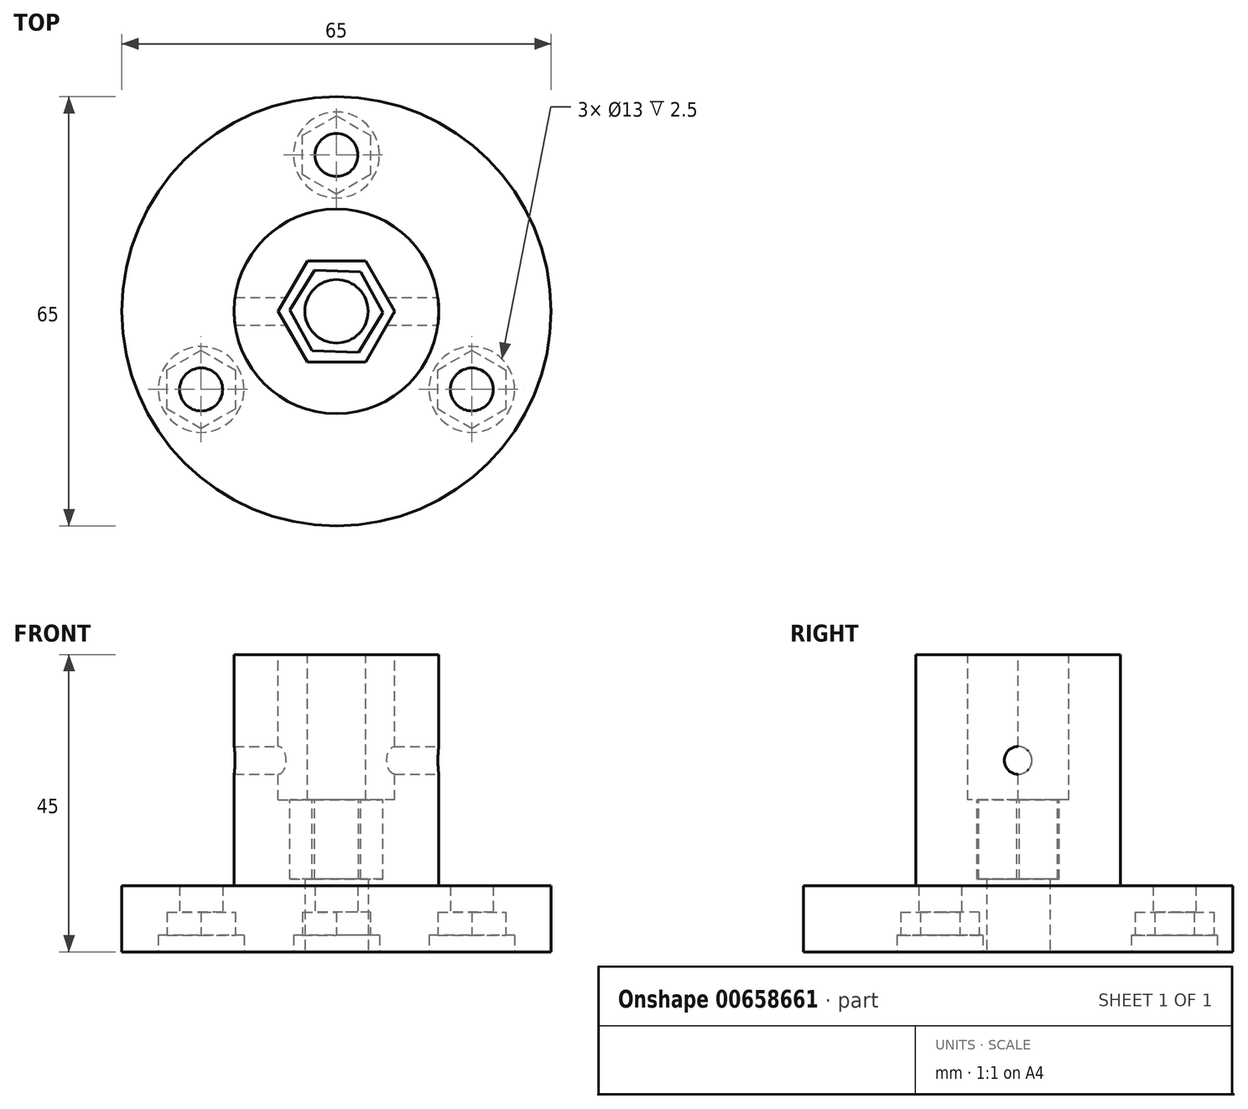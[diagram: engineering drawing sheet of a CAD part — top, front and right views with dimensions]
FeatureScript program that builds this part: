
annotation { "Feature Type Name" : "Feature", "Feature Type Description" : "" }
export const myFeature = defineFeature(function(context is Context, id is Id, definition is map)
    precondition{}
    {
        {
            var Q0;
            Q0=qCreatedBy(makeId("Top.planeOp"),FACE);
            var sketch = newSketch(context, id + "F0", { "sketchPlane" : qUnion([Q0])});
            skCircle(sketch, "E0", {"center": v(0, 0) * mm, "radius": 32.5 * mm});
            skSolve(sketch);
        }
        {
            var Q0;
            Q0=makeQuery(id+"F0.imprint","IMPRINT",FACE,{"disambiguationData":[TD([[makeQuery(id+"F0.imprint","IMPRINT",EDGE,{"derivedFrom":sQuery(id+"F0.wireOp",EDGE,"E0")}),1.0]])]});
            extrude(context, id + "F1", {"entities" : qUnion([Q0]), "depth" : 10 * mm});
        }
        {
            var Q0;
            Q0=makeQuery(id+"F1.opExtrude","CAP_FACE",FACE,{"disambiguationData":[OSD([sQuery(id+"F0.wireOp",EDGE,"E0")])],"isStart":false});
            var sketch = newSketch(context, id + "F2", { "sketchPlane" : qUnion([Q0])});
            skCircle(sketch, "E1", {"center": v(0, 0) * mm, "radius": 15.5 * mm});
            skSolve(sketch);
        }
        {
            var Q0;
            Q0=makeQuery(id+"F2.imprint","IMPRINT",FACE,{"disambiguationData":[TD([[makeQuery(id+"F2.imprint","IMPRINT",EDGE,{"derivedFrom":sQuery(id+"F2.wireOp",EDGE,"E1")}),1.0]])]});
            extrude(context, id + "F3", {"entities" : qUnion([Q0]), "operationType" : NewBodyOperationType.ADD, "depth" : 35 * mm});
        }
        {
            var Q0;
            Q0=qCreatedBy(makeId("Top.planeOp"),FACE);
            var sketch = newSketch(context, id + "F4", { "sketchPlane" : qUnion([Q0])});
            skCircle(sketch, "E2", {"center": v(0, 0) * mm, "radius": 30 * mm});
            skSolve(sketch);
        }
        {
            var Q0;
            Q0=makeQuery(id+"F4.imprint","IMPRINT",FACE,{"disambiguationData":[TD([[makeQuery(id+"F4.imprint","IMPRINT",EDGE,{"derivedFrom":sQuery(id+"F4.wireOp",EDGE,"E2")}),1.0]])]});
            var sketch = newSketch(context, id + "F5", { "sketchPlane" : qUnion([Q0])});
            skCircle(sketch, "E3", {"center": v(0, 0) * mm, "radius": 4.8 * mm});
            skSolve(sketch);
        }
        {
            var Q0;
            Q0=makeQuery(id+"F5.imprint","IMPRINT",FACE,{"disambiguationData":[TD([[makeQuery(id+"F5.imprint","IMPRINT",EDGE,{"derivedFrom":sQuery(id+"F5.wireOp",EDGE,"E3")}),1.0]])]});
            extrude(context, id + "F6", {"entities" : qUnion([Q0]), "operationType" : NewBodyOperationType.REMOVE, "endBound" : BoundingType.THROUGH_ALL, "depth" : 25 * mm});
        }
        {
            var Q0;
            Q0=makeQuery(id+"F3.opExtrude","CAP_FACE",FACE,{"disambiguationData":[OSD([sQuery(id+"F2.wireOp",EDGE,"E1")])],"isStart":false});
            var sketch = newSketch(context, id + "F7", { "sketchPlane" : qUnion([Q0])});
            skCircle(sketch, "E4.cCircle", {"center": v(0, 0) * mm, "radius": 6.1 * mm, "construction": true});
            skLineSegment(sketch, "E4.0", {"start": v(7.04, -0.2) * mm, "end": v(3.34, -6.2) * mm});
            skLineSegment(sketch, "E4.1", {"start": v(3.34, -6.2) * mm, "end": v(-3.7, -6) * mm});
            skLineSegment(sketch, "E4.2", {"start": v(-3.7, -6) * mm, "end": v(-7.04, 0.2) * mm});
            skLineSegment(sketch, "E4.3", {"start": v(-7.04, 0.2) * mm, "end": v(-3.34, 6.2) * mm});
            skLineSegment(sketch, "E4.4", {"start": v(-3.34, 6.2) * mm, "end": v(3.7, 6) * mm});
            skLineSegment(sketch, "E4.5", {"start": v(3.7, 6) * mm, "end": v(7.04, -0.2) * mm});
            skPoint(sketch, "E4.0.midPoint", {"position": v(5.2, -3.2) * mm});
            skSolve(sketch);
        }
        {
            var Q0;
            Q0=makeQuery(id+"F7.imprint","IMPRINT",FACE,{"disambiguationData":[TD([[makeQuery(id+"F7.imprint","IMPRINT",EDGE,{"derivedFrom":sQuery(id+"F7.wireOp",EDGE,"E4.0")}),-1.0]])]});
            extrude(context, id + "F8", {"entities" : qUnion([Q0]), "operationType" : NewBodyOperationType.REMOVE, "oppositeDirection" : true, "depth" : 34 * mm});
        }
        {
            var Q0;
            Q0=makeQuery(id+"F3.opExtrude","CAP_FACE",FACE,{"disambiguationData":[OSD([sQuery(id+"F2.wireOp",EDGE,"E1")])],"isStart":false});
            var sketch = newSketch(context, id + "F9", { "sketchPlane" : qUnion([Q0])});
            skCircle(sketch, "E5.cCircle", {"center": v(0, 0) * mm, "radius": 7.65 * mm, "construction": true});
            skLineSegment(sketch, "E5.0", {"start": v(4.42, -7.65) * mm, "end": v(-4.42, -7.65) * mm});
            skLineSegment(sketch, "E5.1", {"start": v(-4.42, -7.65) * mm, "end": v(-8.83, 0) * mm});
            skLineSegment(sketch, "E5.2", {"start": v(-8.83, 0) * mm, "end": v(-4.42, 7.65) * mm});
            skLineSegment(sketch, "E5.3", {"start": v(-4.42, 7.65) * mm, "end": v(4.42, 7.65) * mm});
            skLineSegment(sketch, "E5.4", {"start": v(4.42, 7.65) * mm, "end": v(8.83, 0) * mm});
            skLineSegment(sketch, "E5.5", {"start": v(8.83, 0) * mm, "end": v(4.42, -7.65) * mm});
            skPoint(sketch, "E5.0.midPoint", {"position": v(0, -7.65) * mm});
            skSolve(sketch);
        }
        {
            var Q0;
            Q0=makeQuery(id+"F9.imprint","IMPRINT",FACE,{"disambiguationData":[TD([[makeQuery(id+"F9.imprint","IMPRINT",EDGE,{"derivedFrom":sQuery(id+"F9.wireOp",EDGE,"E5.0")}),-1.0]])]});
            extrude(context, id + "F10", {"entities" : qUnion([Q0]), "operationType" : NewBodyOperationType.REMOVE, "oppositeDirection" : true, "depth" : 22 * mm});
        }
        {
            var Q0;
            Q0=makeQuery(id+"F4.imprint","IMPRINT",FACE,{"disambiguationData":[TD([[makeQuery(id+"F4.imprint","IMPRINT",EDGE,{"derivedFrom":sQuery(id+"F4.wireOp",EDGE,"E2")}),1.0]])]});
            var sketch = newSketch(context, id + "F11", { "sketchPlane" : qUnion([Q0])});
            skCircle(sketch, "E6.cCircle", {"center": v(0, 0) * mm, "radius": 11.84 * mm, "construction": true});
            skLineSegment(sketch, "E6.0", {"start": v(0, 23.67) * mm, "end": v(20.5, -11.84) * mm, "construction": true});
            skLineSegment(sketch, "E6.1", {"start": v(20.5, -11.84) * mm, "end": v(-20.5, -11.84) * mm, "construction": true});
            skLineSegment(sketch, "E6.2", {"start": v(-20.5, -11.84) * mm, "end": v(0, 23.67) * mm, "construction": true});
            skPoint(sketch, "E6.0.midPoint", {"position": v(10.25, 5.92) * mm});
            skCircle(sketch, "E7.cCircle", {"center": v(-20.5, -11.84) * mm, "radius": 5.15 * mm, "construction": true});
            skLineSegment(sketch, "E7.0", {"start": v(-20.5, -5.89) * mm, "end": v(-15.35, -8.86) * mm});
            skLineSegment(sketch, "E7.1", {"start": v(-15.35, -8.86) * mm, "end": v(-15.35, -14.8) * mm});
            skLineSegment(sketch, "E7.2", {"start": v(-15.35, -14.8) * mm, "end": v(-20.5, -17.78) * mm});
            skLineSegment(sketch, "E7.3", {"start": v(-20.5, -17.78) * mm, "end": v(-25.65, -14.8) * mm});
            skLineSegment(sketch, "E7.4", {"start": v(-25.65, -14.8) * mm, "end": v(-25.65, -8.86) * mm});
            skLineSegment(sketch, "E7.5", {"start": v(-25.65, -8.86) * mm, "end": v(-20.5, -5.89) * mm});
            skPoint(sketch, "E7.0.midPoint", {"position": v(-17.93, -7.38) * mm});
            skLineSegment(sketch, "E8.1.0", {"start": v(25.65, -8.86) * mm, "end": v(25.65, -14.8) * mm});
            skLineSegment(sketch, "E8.1.1", {"start": v(25.65, -14.8) * mm, "end": v(20.5, -17.78) * mm});
            skLineSegment(sketch, "E8.1.2", {"start": v(20.5, -17.78) * mm, "end": v(15.35, -14.8) * mm});
            skLineSegment(sketch, "E8.1.3", {"start": v(15.35, -14.8) * mm, "end": v(15.35, -8.86) * mm});
            skLineSegment(sketch, "E8.1.4", {"start": v(15.35, -8.86) * mm, "end": v(20.5, -5.89) * mm});
            skLineSegment(sketch, "E8.1.5", {"start": v(20.5, -5.89) * mm, "end": v(25.65, -8.86) * mm});
            skLineSegment(sketch, "E8.2.0", {"start": v(-5.15, 26.64) * mm, "end": v(0, 29.62) * mm});
            skLineSegment(sketch, "E8.2.1", {"start": v(0, 29.62) * mm, "end": v(5.15, 26.64) * mm});
            skLineSegment(sketch, "E8.2.2", {"start": v(5.15, 26.64) * mm, "end": v(5.15, 20.7) * mm});
            skLineSegment(sketch, "E8.2.3", {"start": v(5.15, 20.7) * mm, "end": v(0, 17.72) * mm});
            skLineSegment(sketch, "E8.2.4", {"start": v(0, 17.72) * mm, "end": v(-5.15, 20.7) * mm});
            skLineSegment(sketch, "E8.2.5", {"start": v(-5.15, 20.7) * mm, "end": v(-5.15, 26.64) * mm});
            skSolve(sketch);
        }
        {
            var Q0;
            Q0=makeQuery(id+"F11.imprint","IMPRINT",FACE,{"disambiguationData":[TD([[makeQuery(id+"F11.imprint","IMPRINT",EDGE,{"derivedFrom":sQuery(id+"F11.wireOp",EDGE,"E7.0")}),-1.0]])]});
            var Q1;
            Q1=makeQuery(id+"F11.imprint","IMPRINT",FACE,{"disambiguationData":[TD([[makeQuery(id+"F11.imprint","IMPRINT",EDGE,{"derivedFrom":sQuery(id+"F11.wireOp",EDGE,"E8.2.0")}),-1.0]])]});
            var Q2;
            Q2=makeQuery(id+"F11.imprint","IMPRINT",FACE,{"disambiguationData":[TD([[makeQuery(id+"F11.imprint","IMPRINT",EDGE,{"derivedFrom":sQuery(id+"F11.wireOp",EDGE,"E8.1.0")}),-1.0]])]});
            extrude(context, id + "F12", {"entities" : qUnion([Q0, Q1, Q2]), "operationType" : NewBodyOperationType.REMOVE, "depth" : 6 * mm});
        }
        {
            var Q0;
            Q0=qCreatedBy(makeId("Right.planeOp"),FACE);
            var sketch = newSketch(context, id + "F13", { "sketchPlane" : qUnion([Q0])});
            skLineSegment(sketch, "E9", {"start": v(-15.5, 10) * mm, "end": v(-15.5, 45) * mm});
            skLineSegment(sketch, "E10", {"start": v(15.5, 45) * mm, "end": v(15.5, 10) * mm});
            skLineSegment(sketch, "E11", {"start": v(-32.5, 0) * mm, "end": v(-32.5, 10) * mm});
            skLineSegment(sketch, "E12", {"start": v(32.5, 10) * mm, "end": v(32.5, 0) * mm});
            skCircle(sketch, "E13", {"center": v(0, 29) * mm, "radius": 2.1 * mm});
            skSolve(sketch);
        }
        {
            var Q0;
            Q0=makeQuery(id+"F13.imprint","IMPRINT",FACE,{"disambiguationData":[TD([[makeQuery(id+"F13.imprint","IMPRINT",EDGE,{"derivedFrom":sQuery(id+"F13.wireOp",EDGE,"E13")}),1.0]])]});
            extrude(context, id + "F14", {"entities" : qUnion([Q0]), "operationType" : NewBodyOperationType.REMOVE, "oppositeDirection" : true, "depth" : 50 * mm, "symmetric" : true});
        }
        {
            var Q0;
            Q0=makeQuery(id+"F4.imprint","IMPRINT",FACE,{"disambiguationData":[TD([[makeQuery(id+"F4.imprint","IMPRINT",EDGE,{"derivedFrom":sQuery(id+"F4.wireOp",EDGE,"E2")}),1.0]])]});
            var sketch = newSketch(context, id + "F15", { "sketchPlane" : qUnion([Q0])});
            skCircle(sketch, "E14.0.0", {"center": v(0, 0) * mm, "radius": 30 * mm});
            skPoint(sketch, "E15.0", {"position": v(-20.5, -17.78) * mm});
            skPoint(sketch, "E16.0", {"position": v(-20.5, -5.89) * mm});
            skLineSegment(sketch, "E17", {"start": v(-20.5, -17.78) * mm, "end": v(-20.5, -5.89) * mm, "construction": true});
            skPoint(sketch, "E18", {"position": v(-20.5, -11.84) * mm});
            skCircle(sketch, "E19", {"center": v(0, 0) * mm, "radius": 23.67 * mm, "construction": true});
            skCircle(sketch, "E20", {"center": v(-20.5, -11.84) * mm, "radius": 3.25 * mm});
            skCircle(sketch, "E21.1.0", {"center": v(20.5, -11.84) * mm, "radius": 3.25 * mm});
            skCircle(sketch, "E21.2.0", {"center": v(0, 23.67) * mm, "radius": 3.25 * mm});
            skSolve(sketch);
        }
        {
            var Q0;
            Q0=makeQuery(id+"F15.imprint","IMPRINT",FACE,{"disambiguationData":[TD([[makeQuery(id+"F15.imprint","IMPRINT",EDGE,{"derivedFrom":sQuery(id+"F15.wireOp",EDGE,"E20")}),1.0]])]});
            var Q1;
            Q1=makeQuery(id+"F15.imprint","IMPRINT",FACE,{"disambiguationData":[TD([[makeQuery(id+"F15.imprint","IMPRINT",EDGE,{"derivedFrom":sQuery(id+"F15.wireOp",EDGE,"E21.2.0")}),1.0]])]});
            var Q2;
            Q2=makeQuery(id+"F15.imprint","IMPRINT",FACE,{"disambiguationData":[TD([[makeQuery(id+"F15.imprint","IMPRINT",EDGE,{"derivedFrom":sQuery(id+"F15.wireOp",EDGE,"E21.1.0")}),1.0]])]});
            extrude(context, id + "F16", {"entities" : qUnion([Q0, Q1, Q2]), "operationType" : NewBodyOperationType.REMOVE, "endBound" : BoundingType.THROUGH_ALL, "depth" : 25 * mm});
        }
        {
            var Q0;
            Q0=makeQuery(id+"F4.imprint","IMPRINT",FACE,{"disambiguationData":[TD([[makeQuery(id+"F4.imprint","IMPRINT",EDGE,{"derivedFrom":sQuery(id+"F4.wireOp",EDGE,"E2")}),1.0]])]});
            var sketch = newSketch(context, id + "F17", { "sketchPlane" : qUnion([Q0])});
            skCircle(sketch, "E22.0", {"center": v(-20.5, -11.84) * mm, "radius": 3.25 * mm});
            skCircle(sketch, "E23", {"center": v(0, 0) * mm, "radius": 23.67 * mm, "construction": true});
            skCircle(sketch, "E24", {"center": v(-20.5, -11.84) * mm, "radius": 6.5 * mm});
            skCircle(sketch, "E25.1.0", {"center": v(20.5, -11.84) * mm, "radius": 6.5 * mm});
            skCircle(sketch, "E25.2.0", {"center": v(0, 23.67) * mm, "radius": 6.5 * mm});
            skSolve(sketch);
        }
        {
            var Q0;
            Q0=makeQuery(id+"F17.imprint","IMPRINT",FACE,{"disambiguationData":[TD([[makeQuery(id+"F17.imprint","IMPRINT",EDGE,{"derivedFrom":sQuery(id+"F17.wireOp",EDGE,"E22.0")}),-1.0]])]});
            var Q1;
            {var subQ0=sQuery(id+"F17.wireOp",EDGE,"E25.2.0");var subQ1=makeQuery(id+"F4.imprint","IMPRINT",EDGE,{"derivedFrom":sQuery(id+"F4.wireOp",EDGE,"E2")});var subQ2=makeQuery(id+"F17.imprint","INTERSECT",VERTEX,{"disambiguationData":[OD(0.0)],"derivedFrom":[subQ1,subQ0]});Q1=makeQuery(id+"F17.imprint","IMPRINT",FACE,{"disambiguationData":[TD([[makeQuery(id+"F17.imprint","IMPRINT",EDGE,{"disambiguationData":[TD([[subQ2,-1.0]])],"derivedFrom":subQ0}),1.0]])]});}
            var Q2;
            {var subQ0=sQuery(id+"F17.wireOp",EDGE,"E25.1.0");var subQ1=makeQuery(id+"F4.imprint","IMPRINT",EDGE,{"derivedFrom":sQuery(id+"F4.wireOp",EDGE,"E2")});var subQ2=makeQuery(id+"F17.imprint","INTERSECT",VERTEX,{"disambiguationData":[OD(0.0)],"derivedFrom":[subQ1,subQ0]});Q2=makeQuery(id+"F17.imprint","IMPRINT",FACE,{"disambiguationData":[TD([[makeQuery(id+"F17.imprint","IMPRINT",EDGE,{"disambiguationData":[TD([[subQ2,1.0]])],"derivedFrom":subQ0}),1.0]])]});}
            var Q3;
            {var subQ0=sQuery(id+"F17.wireOp",EDGE,"E25.1.0");var subQ1=makeQuery(id+"F4.imprint","IMPRINT",EDGE,{"derivedFrom":sQuery(id+"F4.wireOp",EDGE,"E2")});var subQ2=makeQuery(id+"F17.imprint","INTERSECT",VERTEX,{"disambiguationData":[OD(0.0)],"derivedFrom":[subQ1,subQ0]});Q3=makeQuery(id+"F17.imprint","IMPRINT",FACE,{"disambiguationData":[TD([[makeQuery(id+"F17.imprint","IMPRINT",EDGE,{"disambiguationData":[TD([[subQ2,-1.0]])],"derivedFrom":subQ0}),1.0]])]});}
            var Q4;
            {var subQ0=sQuery(id+"F17.wireOp",EDGE,"E24");var subQ1=makeQuery(id+"F4.imprint","IMPRINT",EDGE,{"derivedFrom":sQuery(id+"F4.wireOp",EDGE,"E2")});var subQ2=makeQuery(id+"F17.imprint","INTERSECT",VERTEX,{"disambiguationData":[OD(0.0)],"derivedFrom":[subQ1,subQ0]});Q4=makeQuery(id+"F17.imprint","IMPRINT",FACE,{"disambiguationData":[TD([[makeQuery(id+"F17.imprint","IMPRINT",EDGE,{"disambiguationData":[TD([[subQ2,-1.0]])],"derivedFrom":subQ0}),1.0]])]});}
            var Q5;
            {var subQ0=sQuery(id+"F17.wireOp",EDGE,"E25.2.0");var subQ1=makeQuery(id+"F4.imprint","IMPRINT",EDGE,{"derivedFrom":sQuery(id+"F4.wireOp",EDGE,"E2")});var subQ2=makeQuery(id+"F17.imprint","INTERSECT",VERTEX,{"disambiguationData":[OD(0.0)],"derivedFrom":[subQ1,subQ0]});Q5=makeQuery(id+"F17.imprint","IMPRINT",FACE,{"disambiguationData":[TD([[makeQuery(id+"F17.imprint","IMPRINT",EDGE,{"disambiguationData":[TD([[subQ2,1.0]])],"derivedFrom":subQ0}),1.0]])]});}
            extrude(context, id + "F18", {"entities" : qUnion([Q0, Q1, Q2, Q3, Q4, Q5]), "operationType" : NewBodyOperationType.REMOVE, "depth" : 2.5 * mm});
        }
    });
